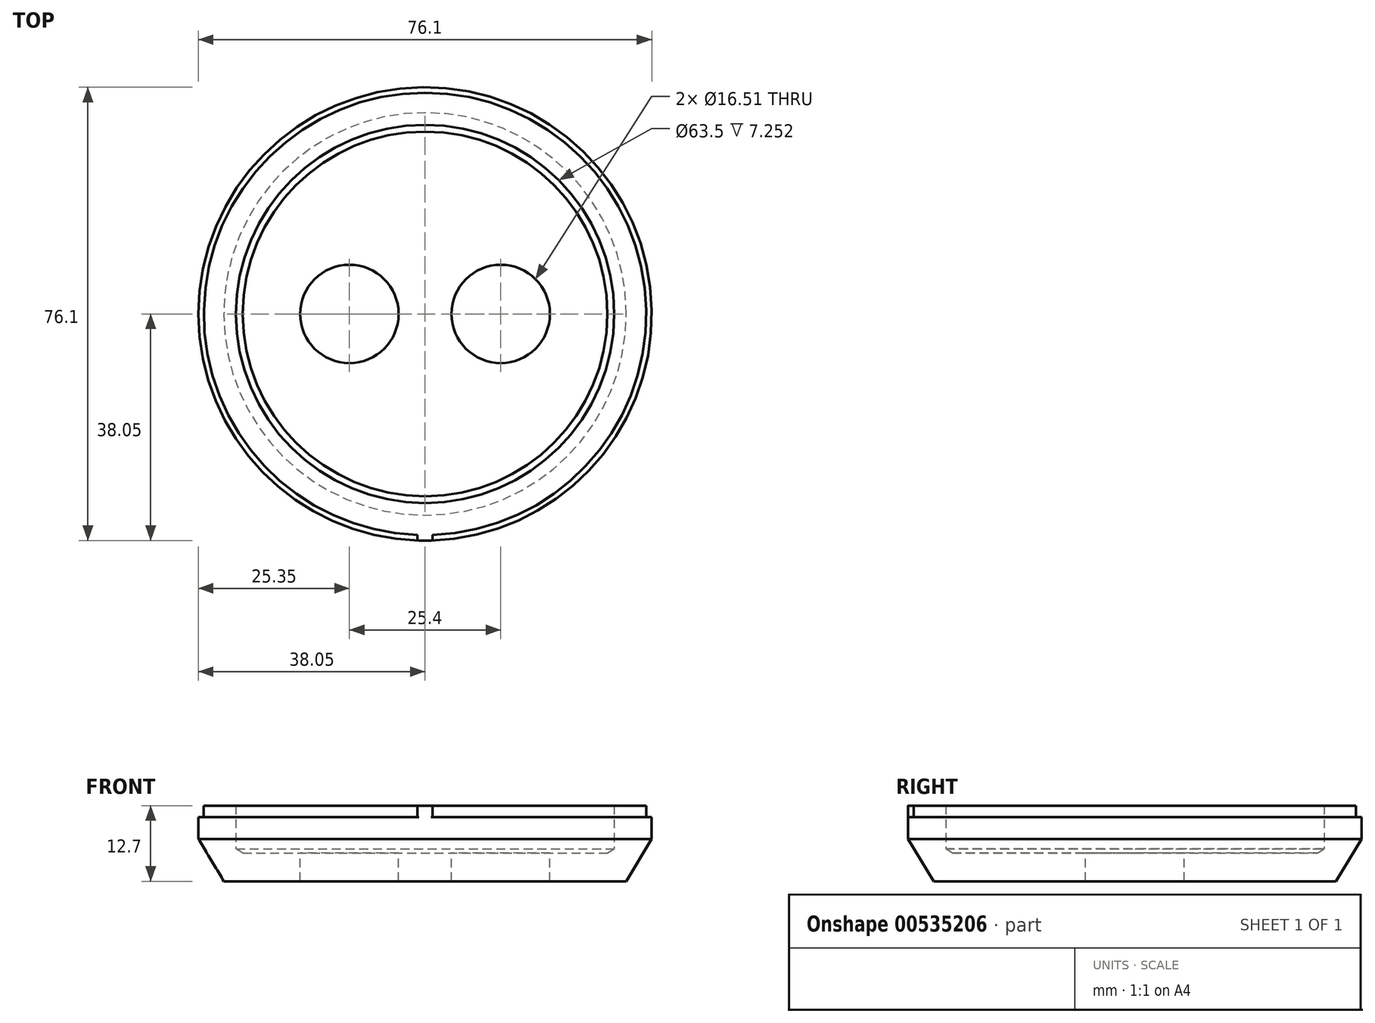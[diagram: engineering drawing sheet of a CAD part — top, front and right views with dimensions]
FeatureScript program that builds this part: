
annotation { "Feature Type Name" : "Feature", "Feature Type Description" : "" }
export const myFeature = defineFeature(function(context is Context, id is Id, definition is map)
    precondition{}
    {
        {
            var Q0;
            Q0=qCreatedBy(makeId("Front.planeOp"),FACE);
            var sketch = newSketch(context, id + "F0", { "sketchPlane" : qUnion([Q0])});
            skLineSegment(sketch, "E0", {"start": v(0, 0) * mm, "end": v(0, 4.76) * mm});
            skLineSegment(sketch, "E1", {"start": v(-31.75, 12.7) * mm, "end": v(-37.13, 12.7) * mm});
            skLineSegment(sketch, "E2", {"start": v(-37.13, 12.7) * mm, "end": v(-37.13, 10.8) * mm});
            skLineSegment(sketch, "E3", {"start": v(-37.13, 10.8) * mm, "end": v(-38.05, 10.8) * mm});
            skLineSegment(sketch, "E4", {"start": v(-38.05, 10.8) * mm, "end": v(-38.05, 7.11) * mm});
            skLineSegment(sketch, "E5", {"start": v(-38.05, 7.11) * mm, "end": v(-33.78, 0) * mm});
            skLineSegment(sketch, "E6", {"start": v(-33.78, 0) * mm, "end": v(0, 0) * mm});
            skLineSegment(sketch, "E7", {"start": v(-31.75, 12.7) * mm, "end": v(-31.75, 5.45) * mm});
            skLineSegment(sketch, "E8", {"start": v(-31.75, 5.45) * mm, "end": v(-30.6, 4.76) * mm});
            skLineSegment(sketch, "E9", {"start": v(-30.6, 4.76) * mm, "end": v(0, 4.76) * mm});
            skSolve(sketch);
        }
        {
            var Q0;
            Q0 = qSketchRegion(id + "F0", true);
            var Q1;
            Q1=sQuery(id+"F0.wireOp",EDGE,"E0");
            revolve(context, id + "F1", {"entities" : qUnion([Q0]), "axis" : qUnion([Q1]), "revolveType" : RevolveType.FULL});
        }
        {
            var Q0;
            Q0=makeQuery(id+"F1.opRevolve","SWEPT_FACE",FACE,{"disambiguationData":[OSD([sQuery(id+"F0.wireOp",EDGE,"E9")])]});
            var sketch = newSketch(context, id + "F2", { "sketchPlane" : qUnion([Q0])});
            skCircle(sketch, "E10", {"center": v(-12.7, 0) * mm, "radius": 8.26 * mm});
            skCircle(sketch, "E11", {"center": v(12.7, 0) * mm, "radius": 8.26 * mm});
            skSolve(sketch);
        }
        {
            var Q0;
            Q0=makeQuery(id+"F2.imprint","IMPRINT",FACE,{"disambiguationData":[TD([[makeQuery(id+"F2.imprint","IMPRINT",EDGE,{"derivedFrom":sQuery(id+"F2.wireOp",EDGE,"E10")}),1.0]])]});
            var Q1;
            Q1=makeQuery(id+"F2.imprint","IMPRINT",FACE,{"disambiguationData":[TD([[makeQuery(id+"F2.imprint","IMPRINT",EDGE,{"derivedFrom":sQuery(id+"F2.wireOp",EDGE,"E11")}),1.0]])]});
            extrude(context, id + "F3", {"entities" : qUnion([Q0, Q1]), "operationType" : NewBodyOperationType.REMOVE, "oppositeDirection" : true, "depth" : 25.4 * mm, "offsetDistance" : 25.4 * mm});
        }
        {
            var Q0;
            Q0=makeQuery(id+"F1.opRevolve","SWEPT_FACE",FACE,{"disambiguationData":[OSD([sQuery(id+"F0.wireOp",EDGE,"E1")])]});
            var sketch = newSketch(context, id + "F4", { "sketchPlane" : qUnion([Q0])});
            skCircle(sketch, "E12.0", {"center": v(0, 0) * mm, "radius": 37.13 * mm});
            skCircle(sketch, "E13.0", {"center": v(0, 0) * mm, "radius": 38.05 * mm});
            skLineSegment(sketch, "E14", {"start": v(-1.27, -37.11) * mm, "end": v(-1.27, -38.03) * mm});
            skLineSegment(sketch, "E15", {"start": v(1.27, -37.11) * mm, "end": v(1.27, -38.03) * mm});
            skSolve(sketch);
        }
        {
            var Q0;
            {var subQ0=sQuery(id+"F4.wireOp",EDGE,"E14");Q0=makeQuery(id+"F4.imprint","IMPRINT",FACE,{"disambiguationData":[TD([[makeQuery(id+"F4.imprint","IMPRINT",EDGE,{"derivedFrom":subQ0}),1.0]])]});}
            extrude(context, id + "F5", {"entities" : qUnion([Q0]), "operationType" : NewBodyOperationType.ADD, "endBound" : BoundingType.UP_TO_NEXT, "oppositeDirection" : true, "depth" : 25.4 * mm, "offsetDistance" : 25.4 * mm});
        }
        {
            var Q0;
            Q0=makeQuery(id+"F5.opExtrude","SWEPT_EDGE",EDGE,{"disambiguationData":[OSD([sQuery(id+"F4.wireOp",EDGE,"E12.0"),sQuery(id+"F4.wireOp",EDGE,"E15")])]});
            var Q1;
            Q1=makeQuery(id+"F5.opExtrude","SWEPT_EDGE",EDGE,{"disambiguationData":[OSD([sQuery(id+"F4.wireOp",EDGE,"E13.0"),sQuery(id+"F4.wireOp",EDGE,"E15")])]});
            var Q2;
            Q2=makeQuery(id+"F5.opExtrude","SWEPT_EDGE",EDGE,{"disambiguationData":[OSD([sQuery(id+"F4.wireOp",EDGE,"E13.0"),sQuery(id+"F4.wireOp",EDGE,"E14")])]});
            var Q3;
            Q3=makeQuery(id+"F5.opExtrude","SWEPT_EDGE",EDGE,{"disambiguationData":[OSD([sQuery(id+"F4.wireOp",EDGE,"E12.0"),sQuery(id+"F4.wireOp",EDGE,"E14")])]});
            fillet(context, id + "F6", {"entities" : qUnion([Q0, Q1, Q2, Q3]), "radius" : 0.25 * mm, "tangentPropagation" : true, "allowEdgeOverflow" : false});
        }
    });
